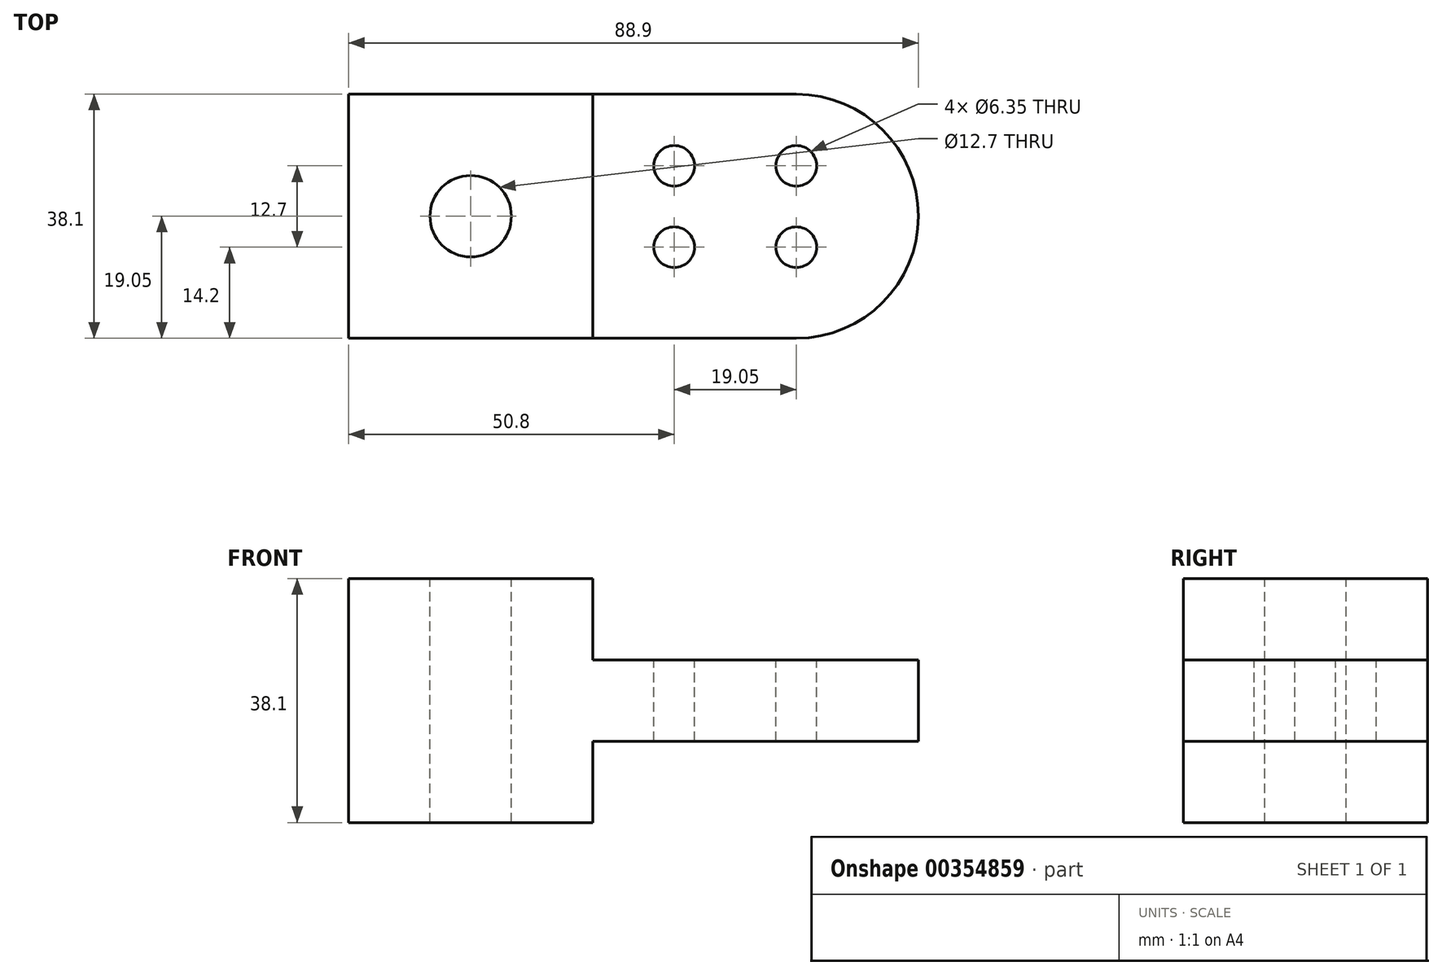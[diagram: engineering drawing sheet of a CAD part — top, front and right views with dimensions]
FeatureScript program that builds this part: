
annotation { "Feature Type Name" : "Feature", "Feature Type Description" : "" }
export const myFeature = defineFeature(function(context is Context, id is Id, definition is map)
    precondition{}
    {
        {
            var Q0;
            Q0=qCreatedBy(makeId("Top.planeOp"),FACE);
            var sketch = newSketch(context, id + "F0", { "sketchPlane" : qUnion([Q0])});
            skLineSegment(sketch, "E0", {"start": v(0, 38.1) * mm, "end": v(31.75, 38.1) * mm});
            skLineSegment(sketch, "E1", {"start": v(0, 0) * mm, "end": v(31.75, 0) * mm});
            skArc(sketch, "E2", {"start": v(31.75, 38.1) * mm, "mid": v(50.8, 19.05) * mm, "end": v(31.75, 0) * mm});
            skLineSegment(sketch, "E3", {"start": v(0, 38.1) * mm, "end": v(0, 0) * mm});
            skSolve(sketch);
        }
        {
            var Q0;
            Q0=makeQuery(id+"F0.imprint","IMPRINT",FACE,{"disambiguationData":[TD([[makeQuery(id+"F0.imprint","IMPRINT",EDGE,{"derivedFrom":sQuery(id+"F0.wireOp",EDGE,"E0")}),-1.0]])]});
            extrude(context, id + "F1", {"entities" : qUnion([Q0]), "depth" : 12.7 * mm});
        }
        {
            var Q0;
            Q0=makeQuery(id+"F1.opExtrude","SWEPT_FACE",FACE,{"disambiguationData":[OSD([sQuery(id+"F0.wireOp",EDGE,"E3")])]});
            var sketch = newSketch(context, id + "F2", { "sketchPlane" : qUnion([Q0])});
            skLineSegment(sketch, "E4.bottom", {"start": v(-38.1, -12.7) * mm, "end": v(0, -12.7) * mm});
            skLineSegment(sketch, "E4.top", {"start": v(-38.1, 25.4) * mm, "end": v(0, 25.4) * mm});
            skLineSegment(sketch, "E4.right", {"start": v(0, -12.7) * mm, "end": v(0, 25.4) * mm});
            skLineSegment(sketch, "E5.0", {"start": v(-38.1, 12.7) * mm, "end": v(-38.1, 0) * mm});
            skLineSegment(sketch, "E6", {"start": v(-38.1, 25.4) * mm, "end": v(-38.1, -12.7) * mm});
            skSolve(sketch);
        }
        {
            var Q0;
            {var subQ0=sQuery(id+"F2.wireOp",EDGE,"E4.top");Q0=makeQuery(id+"F2.imprint","IMPRINT",FACE,{"disambiguationData":[TD([[makeQuery(id+"F2.imprint","IMPRINT",EDGE,{"derivedFrom":subQ0}),-1.0]])]});}
            var Q1;
            {var subQ1=sQuery(id+"F0.wireOp",EDGE,"E3");var subQ2=makeQuery(id+"F1.opExtrude","CAP_EDGE",EDGE,{"disambiguationData":[OSD([subQ1])],"isStart":true});Q1=makeQuery(id+"F2.imprint","IMPRINT",FACE,{"disambiguationData":[TD([[makeQuery(id+"F2.imprint","IMPRINT",EDGE,{"derivedFrom":subQ2}),1.0]])]});}
            var Q2;
            {var subQ0=sQuery(id+"F2.wireOp",EDGE,"E4.bottom");Q2=makeQuery(id+"F2.imprint","IMPRINT",FACE,{"disambiguationData":[TD([[makeQuery(id+"F2.imprint","IMPRINT",EDGE,{"derivedFrom":subQ0}),1.0]])]});}
            extrude(context, id + "F3", {"entities" : qUnion([Q0, Q1, Q2]), "operationType" : NewBodyOperationType.ADD, "depth" : 38.1 * mm});
        }
        {
            var Q0;
            Q0=makeQuery(id+"F3.opExtrude","SWEPT_FACE",FACE,{"disambiguationData":[OSD([sQuery(id+"F2.wireOp",EDGE,"E4.top")])]});
            var sketch = newSketch(context, id + "F4", { "sketchPlane" : qUnion([Q0])});
            skCircle(sketch, "E7", {"center": v(-19.05, 19.05) * mm, "radius": 6.35 * mm});
            skPoint(sketch, "E8", {"position": v(12.7, 26.9) * mm});
            skPoint(sketch, "E9", {"position": v(31.75, 26.9) * mm});
            skPoint(sketch, "E10", {"position": v(31.75, 14.2) * mm});
            skPoint(sketch, "E11", {"position": v(12.7, 14.2) * mm});
            skSolve(sketch);
        }
        {
            var Q0;
            Q0=makeQuery(id+"F4.imprint","IMPRINT",FACE,{"disambiguationData":[TD([[makeQuery(id+"F4.imprint","IMPRINT",EDGE,{"derivedFrom":sQuery(id+"F4.wireOp",EDGE,"E7")}),1.0]])]});
            extrude(context, id + "F5", {"entities" : qUnion([Q0]), "operationType" : NewBodyOperationType.REMOVE, "endBound" : BoundingType.THROUGH_ALL, "oppositeDirection" : true, "depth" : 25.4 * mm});
        }
        {
            var Q0;
            Q0=sQuery(id+"F4.wireOp",VERTEX,"E8");
            var Q1;
            Q1=sQuery(id+"F4.wireOp",VERTEX,"E11");
            var Q2;
            Q2=sQuery(id+"F4.wireOp",VERTEX,"E9");
            var Q3;
            Q3=sQuery(id+"F4.wireOp",VERTEX,"E10");
            var Q4;
            Q4=makeQuery(id+"F1.opExtrude","SWEPT_BODY",BODY,{"disambiguationData":[OSD([sQuery(id+"F0.wireOp",EDGE,"E0"),sQuery(id+"F0.wireOp",EDGE,"E1"),sQuery(id+"F0.wireOp",EDGE,"E2"),sQuery(id+"F0.wireOp",EDGE,"E3")])]});
            hole(context, id + "F6", {"style" : HoleStyle.SIMPLE, "endStyle" : HoleEndStyle.THROUGH, "holeDiameter" : 6.35 * mm, "isTappedThrough" : true, "tappedDepth" : 12.7 * mm, "tapClearance" : 3, "locations" : qUnion([Q0, Q1, Q2, Q3]), "scope" : qUnion([Q4])});
        }
    });
